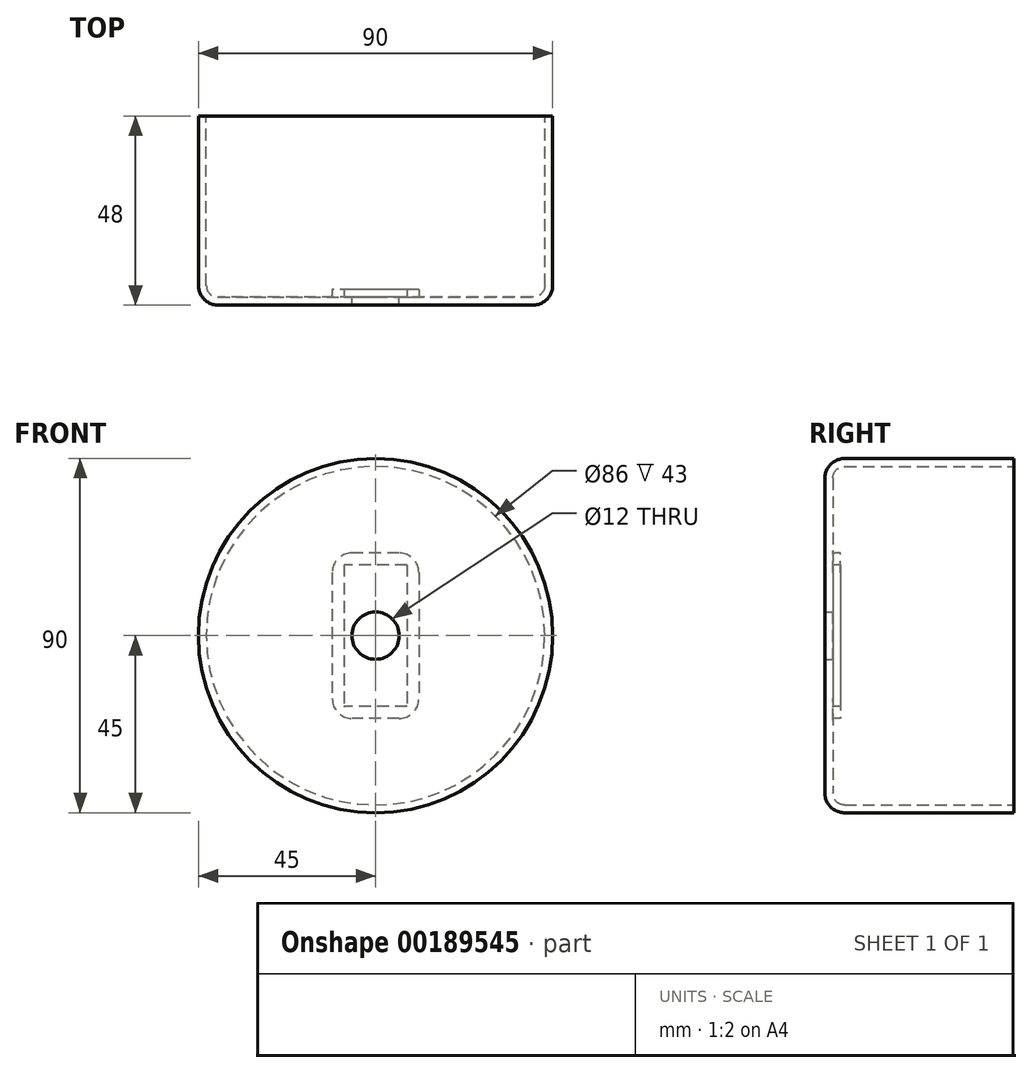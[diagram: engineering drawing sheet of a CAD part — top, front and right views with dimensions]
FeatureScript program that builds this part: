
annotation { "Feature Type Name" : "Feature", "Feature Type Description" : "" }
export const myFeature = defineFeature(function(context is Context, id is Id, definition is map)
    precondition{}
    {
        {
            var Q0;
            Q0=qCreatedBy(makeId("Right.planeOp"),FACE);
            var sketch = newSketch(context, id + "F0", { "sketchPlane" : qUnion([Q0])});
            skLineSegment(sketch, "E0", {"start": v(-21, 0) * mm, "end": v(-23, 0) * mm});
            skLineSegment(sketch, "E1", {"start": v(-23, 0) * mm, "end": v(-23, 40) * mm});
            skLineSegment(sketch, "E2", {"start": v(-18, 45) * mm, "end": v(25, 45) * mm});
            skLineSegment(sketch, "E3", {"start": v(25, 45) * mm, "end": v(25, 40) * mm});
            skLineSegment(sketch, "E4", {"start": v(25, 40) * mm, "end": v(23, 40) * mm});
            skLineSegment(sketch, "E5", {"start": v(23, 40) * mm, "end": v(23, 43) * mm});
            skLineSegment(sketch, "E6", {"start": v(23, 43) * mm, "end": v(17, 43) * mm});
            skLineSegment(sketch, "E7", {"start": v(17, 43) * mm, "end": v(17, 40) * mm});
            skLineSegment(sketch, "E8", {"start": v(17, 40) * mm, "end": v(15, 40) * mm});
            skLineSegment(sketch, "E9", {"start": v(15, 40) * mm, "end": v(15, 43) * mm});
            skLineSegment(sketch, "E10", {"start": v(15, 43) * mm, "end": v(-18, 43) * mm});
            skLineSegment(sketch, "E11", {"start": v(-21, 40) * mm, "end": v(-21, 0) * mm});
            skArc(sketch, "E12.filletArc", {"start": v(-18, 43) * mm, "mid": v(-20.12, 42.12) * mm, "end": v(-21, 40) * mm});
            skArc(sketch, "E13.filletArc", {"start": v(-18, 45) * mm, "mid": v(-21.54, 43.54) * mm, "end": v(-23, 40) * mm});
            skLineSegment(sketch, "E14.bottom", {"start": v(-21, 34.1) * mm, "end": v(-9, 34.1) * mm});
            skLineSegment(sketch, "E14.top", {"start": v(-21, 32.1) * mm, "end": v(-9, 32.1) * mm});
            skLineSegment(sketch, "E14.left", {"start": v(-21, 34.1) * mm, "end": v(-21, 32.1) * mm});
            skLineSegment(sketch, "E14.right", {"start": v(-9, 34.1) * mm, "end": v(-9, 32.1) * mm});
            skLineSegment(sketch, "E15.bottom", {"start": v(-9, 32.1) * mm, "end": v(-11, 32.1) * mm});
            skLineSegment(sketch, "E15.top", {"start": v(-9, 30.6) * mm, "end": v(-11, 30.6) * mm});
            skLineSegment(sketch, "E15.left", {"start": v(-9, 32.1) * mm, "end": v(-9, 30.6) * mm});
            skLineSegment(sketch, "E15.right", {"start": v(-11, 32.1) * mm, "end": v(-11, 30.6) * mm});
            skLineSegment(sketch, "E16.bottom", {"start": v(-12.1, 32.1) * mm, "end": v(-15.1, 32.1) * mm});
            skLineSegment(sketch, "E16.top", {"start": v(-12.1, 30.6) * mm, "end": v(-15.1, 30.6) * mm});
            skLineSegment(sketch, "E16.left", {"start": v(-12.1, 32.1) * mm, "end": v(-12.1, 30.6) * mm});
            skLineSegment(sketch, "E16.right", {"start": v(-15.1, 32.1) * mm, "end": v(-15.1, 30.6) * mm});
            skLineSegment(sketch, "E17.bottom", {"start": v(-16.2, 32.1) * mm, "end": v(-18.2, 32.1) * mm});
            skLineSegment(sketch, "E17.top", {"start": v(-16.2, 30.6) * mm, "end": v(-18.2, 30.6) * mm});
            skLineSegment(sketch, "E17.left", {"start": v(-16.2, 32.1) * mm, "end": v(-16.2, 30.6) * mm});
            skLineSegment(sketch, "E17.right", {"start": v(-18.2, 32.1) * mm, "end": v(-18.2, 30.6) * mm});
            skLineSegment(sketch, "E18", {"start": v(15, 43) * mm, "end": v(17, 43) * mm});
            skLineSegment(sketch, "E19", {"start": v(23, 43) * mm, "end": v(25, 43) * mm});
            skSolve(sketch);
        }
        {
            var Q0;
            Q0=makeQuery(id+"F0.imprint","IMPRINT",FACE,{"disambiguationData":[TD([[makeQuery(id+"F0.imprint","IMPRINT",EDGE,{"derivedFrom":sQuery(id+"F0.wireOp",EDGE,"E0")}),-1.0]])]});
            var Q1;
            Q1=sQuery(id+"F0.wireOp",EDGE,"E0");
            revolve(context, id + "F1", {"entities" : qUnion([Q0]), "axis" : qUnion([Q1]), "revolveType" : RevolveType.FULL});
        }
        {
            var Q0;
            Q0=makeQuery(id+"F1.opRevolve","SWEPT_FACE",FACE,{"disambiguationData":[OSD([sQuery(id+"F0.wireOp",EDGE,"E11")])]});
            var sketch = newSketch(context, id + "F2", { "sketchPlane" : qUnion([Q0])});
            skLineSegment(sketch, "E20.bottom", {"start": v(-8, 18) * mm, "end": v(8, 18) * mm});
            skLineSegment(sketch, "E20.top", {"start": v(-8, -18) * mm, "end": v(8, -18) * mm});
            skLineSegment(sketch, "E20.left", {"start": v(-8, 18) * mm, "end": v(-8, -18) * mm});
            skLineSegment(sketch, "E20.right", {"start": v(8, 18) * mm, "end": v(8, -18) * mm});
            skLineSegment(sketch, "E21.bottom", {"start": v(-11, 21) * mm, "end": v(11, 21) * mm});
            skLineSegment(sketch, "E21.top", {"start": v(-11, -21) * mm, "end": v(11, -21) * mm});
            skLineSegment(sketch, "E21.left", {"start": v(-11, 21) * mm, "end": v(-11, -21) * mm});
            skLineSegment(sketch, "E21.right", {"start": v(11, 21) * mm, "end": v(11, -21) * mm});
            skCircle(sketch, "E22", {"center": v(0, 0) * mm, "radius": 6 * mm});
            skSolve(sketch);
        }
        {
            var Q0;
            {var subQ4=sQuery(id+"F2.wireOp",EDGE,"E20.left");Q0=makeQuery(id+"F2.imprint","IMPRINT",FACE,{"disambiguationData":[TD([[makeQuery(id+"F2.imprint","IMPRINT",EDGE,{"derivedFrom":subQ4}),-1.0]])]});}
            extrude(context, id + "F3", {"entities" : qUnion([Q0]), "operationType" : NewBodyOperationType.ADD, "depth" : 2 * mm});
        }
        {
            var Q0;
            {var subQ0=sQuery(id+"F2.wireOp",EDGE,"E22");var subQ1=makeQuery(id+"F2.imprint","INTERSECT",VERTEX,{"derivedFrom":[sQuery(id+"F2.wireOp",EDGE,"E20.bottom"),subQ0]});Q0=makeQuery(id+"F2.imprint","IMPRINT",FACE,{"disambiguationData":[TD([[makeQuery(id+"F2.imprint","IMPRINT",EDGE,{"disambiguationData":[TD([[subQ1,-1.0]])],"derivedFrom":subQ0}),1.0]])]});}
            extrude(context, id + "F4", {"entities" : qUnion([Q0]), "operationType" : NewBodyOperationType.REMOVE, "oppositeDirection" : true, "depth" : 25 * mm});
        }
        {
            var Q0;
            Q0=makeQuery(id+"F3.opExtrude","SWEPT_EDGE",EDGE,{"disambiguationData":[OSD([sQuery(id+"F2.wireOp",EDGE,"E21.bottom"),sQuery(id+"F2.wireOp",EDGE,"E21.left")])]});
            var Q1;
            Q1=makeQuery(id+"F3.opExtrude","SWEPT_EDGE",EDGE,{"disambiguationData":[OSD([sQuery(id+"F2.wireOp",EDGE,"E21.bottom"),sQuery(id+"F2.wireOp",EDGE,"E21.right")])]});
            var Q2;
            Q2=makeQuery(id+"F3.opExtrude","SWEPT_EDGE",EDGE,{"disambiguationData":[OSD([sQuery(id+"F2.wireOp",EDGE,"E21.top"),sQuery(id+"F2.wireOp",EDGE,"E21.right")])]});
            var Q3;
            Q3=makeQuery(id+"F3.opExtrude","SWEPT_EDGE",EDGE,{"disambiguationData":[OSD([sQuery(id+"F2.wireOp",EDGE,"E21.top"),sQuery(id+"F2.wireOp",EDGE,"E21.left")])]});
            fillet(context, id + "F5", {"entities" : qUnion([Q0, Q1, Q2, Q3]), "radius" : 5 * mm, "tangentPropagation" : true, "allowEdgeOverflow" : false});
        }
        {
            var Q0;
            Q0=makeQuery(id+"F3.boolean.opBoolean","SPLIT",FACE,{"disambiguationData":[TD([makeQuery(id+"F1.opRevolve","SWEPT_FACE",FACE,{"disambiguationData":[OSD([sQuery(id+"F0.wireOp",EDGE,"E12.filletArc")])]})])],"derivedFrom":makeQuery(id+"F1.opRevolve","SWEPT_FACE",FACE,{"disambiguationData":[OSD([sQuery(id+"F0.wireOp",EDGE,"E11")])]})});
            var Q1;
            Q1=makeQuery(id+"F1.opRevolve","SWEPT_FACE",FACE,{"disambiguationData":[OSD([sQuery(id+"F0.wireOp",EDGE,"E5")])]});
            fillet(context, id + "F6", {"entities" : qUnion([Q0, Q1]), "radius" : 0.5 * mm, "tangentPropagation" : true, "allowEdgeOverflow" : false});
        }
        {
            var Q0;
            {var subQ0=makeQuery(id+"F3.opExtrude","SWEPT_FACE",FACE,{"disambiguationData":[OSD([sQuery(id+"F2.wireOp",EDGE,"E20.right")])]});var subQ2=makeQuery(id+"F3.opExtrude","SWEPT_FACE",FACE,{"disambiguationData":[OSD([sQuery(id+"F2.wireOp",EDGE,"E20.bottom")])]});var subQ3=makeQuery(id+"F1.opRevolve","SWEPT_FACE",FACE,{"disambiguationData":[OSD([sQuery(id+"F0.wireOp",EDGE,"E11")])]});Q0=makeQuery(id+"F4.boolean.opBoolean","SPLIT",FACE,{"disambiguationData":[TD([subQ0])],"derivedFrom":makeQuery(id+"F3.boolean.opBoolean","SPLIT",FACE,{"disambiguationData":[TD([subQ2])],"derivedFrom":subQ3})});}
            var Q1;
            {var subQ0=makeQuery(id+"F3.opExtrude","SWEPT_FACE",FACE,{"disambiguationData":[OSD([sQuery(id+"F2.wireOp",EDGE,"E20.left")])]});var subQ2=makeQuery(id+"F3.opExtrude","SWEPT_FACE",FACE,{"disambiguationData":[OSD([sQuery(id+"F2.wireOp",EDGE,"E20.bottom")])]});var subQ3=makeQuery(id+"F1.opRevolve","SWEPT_FACE",FACE,{"disambiguationData":[OSD([sQuery(id+"F0.wireOp",EDGE,"E11")])]});Q1=makeQuery(id+"F4.boolean.opBoolean","SPLIT",FACE,{"disambiguationData":[TD([subQ0])],"derivedFrom":makeQuery(id+"F3.boolean.opBoolean","SPLIT",FACE,{"disambiguationData":[TD([subQ2])],"derivedFrom":subQ3})});}
            var Q2;
            Q2=makeQuery(id+"F1.opRevolve","SWEPT_FACE",FACE,{"disambiguationData":[OSD([sQuery(id+"F0.wireOp",EDGE,"E9")])]});
            var Q3;
            Q3=makeQuery(id+"F1.opRevolve","SWEPT_EDGE",EDGE,{"disambiguationData":[OSD([sQuery(id+"F0.wireOp",EDGE,"E14.bottom"),sQuery(id+"F0.wireOp",EDGE,"E14.right")])]});
            var Q4;
            Q4=makeQuery(id+"F1.opRevolve","SWEPT_EDGE",EDGE,{"disambiguationData":[OSD([sQuery(id+"F0.wireOp",EDGE,"E11"),sQuery(id+"F0.wireOp",EDGE,"E14.bottom"),sQuery(id+"F0.wireOp",EDGE,"E14.left")])]});
            var Q5;
            Q5=makeQuery(id+"F1.opRevolve","SWEPT_EDGE",EDGE,{"disambiguationData":[OSD([sQuery(id+"F0.wireOp",EDGE,"E11"),sQuery(id+"F0.wireOp",EDGE,"E14.top"),sQuery(id+"F0.wireOp",EDGE,"E14.left")])]});
            var Q6;
            Q6=makeQuery(id+"F1.opRevolve","SWEPT_FACE",FACE,{"disambiguationData":[OSD([sQuery(id+"F0.wireOp",EDGE,"E17.top")])]});
            var Q7;
            Q7=makeQuery(id+"F1.opRevolve","SWEPT_FACE",FACE,{"disambiguationData":[OSD([sQuery(id+"F0.wireOp",EDGE,"E16.top")])]});
            var Q8;
            Q8=makeQuery(id+"F1.opRevolve","SWEPT_FACE",FACE,{"disambiguationData":[OSD([sQuery(id+"F0.wireOp",EDGE,"E15.top")])]});
            fillet(context, id + "F7", {"entities" : qUnion([Q0, Q1, Q2, Q3, Q4, Q5, Q6, Q7, Q8]), "radius" : 0.2 * mm, "tangentPropagation" : true, "allowEdgeOverflow" : false});
        }
    });
